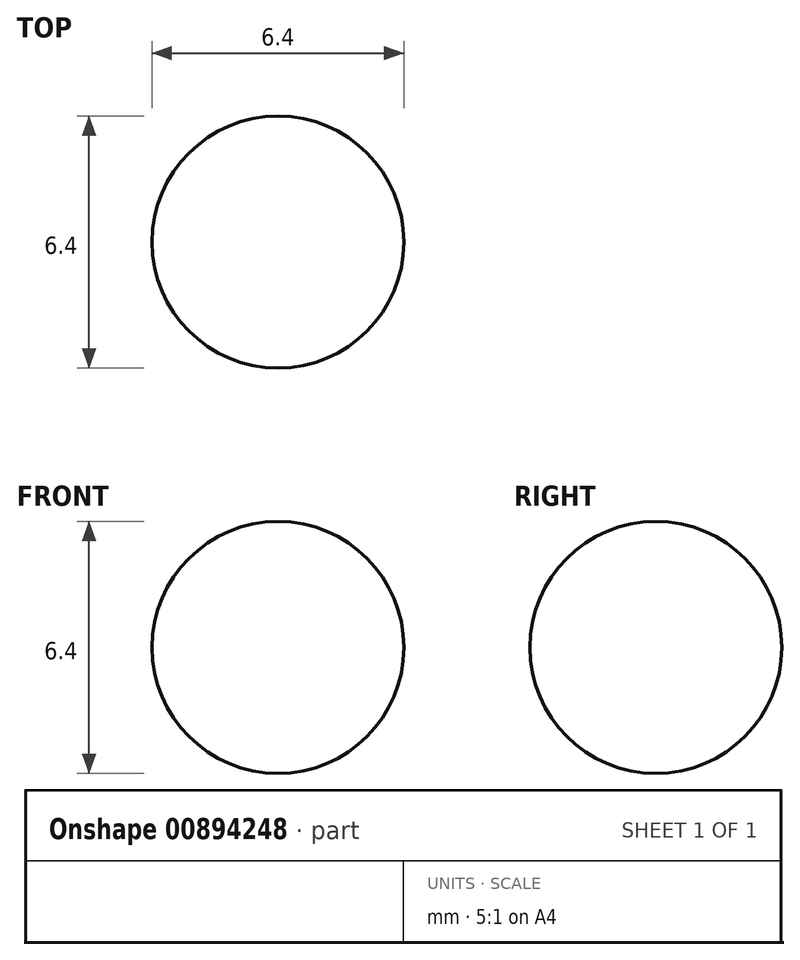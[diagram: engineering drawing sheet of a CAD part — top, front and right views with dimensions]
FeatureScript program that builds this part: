
annotation { "Feature Type Name" : "Feature", "Feature Type Description" : "" }
export const myFeature = defineFeature(function(context is Context, id is Id, definition is map)
    precondition{}
    {
        {
            var Q0;
            Q0=qCreatedBy(makeId("Front.planeOp"),FACE);
            var sketch = newSketch(context, id + "F0", { "sketchPlane" : qUnion([Q0])});
            skLineSegment(sketch, "E0", {"start": v(0, 3.2) * mm, "end": v(0, -3.2) * mm});
            skArc(sketch, "E1", {"start": v(0, -3.2) * mm, "mid": v(3.2, 0) * mm, "end": v(0, 3.2) * mm});
            skSolve(sketch);
        }
        {
            var Q0;
            Q0=makeQuery(id+"F0.imprint","IMPRINT",FACE,{"disambiguationData":[TD([[makeQuery(id+"F0.imprint","IMPRINT",EDGE,{"derivedFrom":sQuery(id+"F0.wireOp",EDGE,"E0")}),1.0]])]});
            var Q1;
            Q1=sQuery(id+"F0.wireOp",EDGE,"E0");
            revolve(context, id + "F1", {"surfaceOperationType" : NewSurfaceOperationType.NEW, "entities" : qUnion([Q0]), "axis" : qUnion([Q1]), "revolveType" : RevolveType.FULL});
        }
    });
